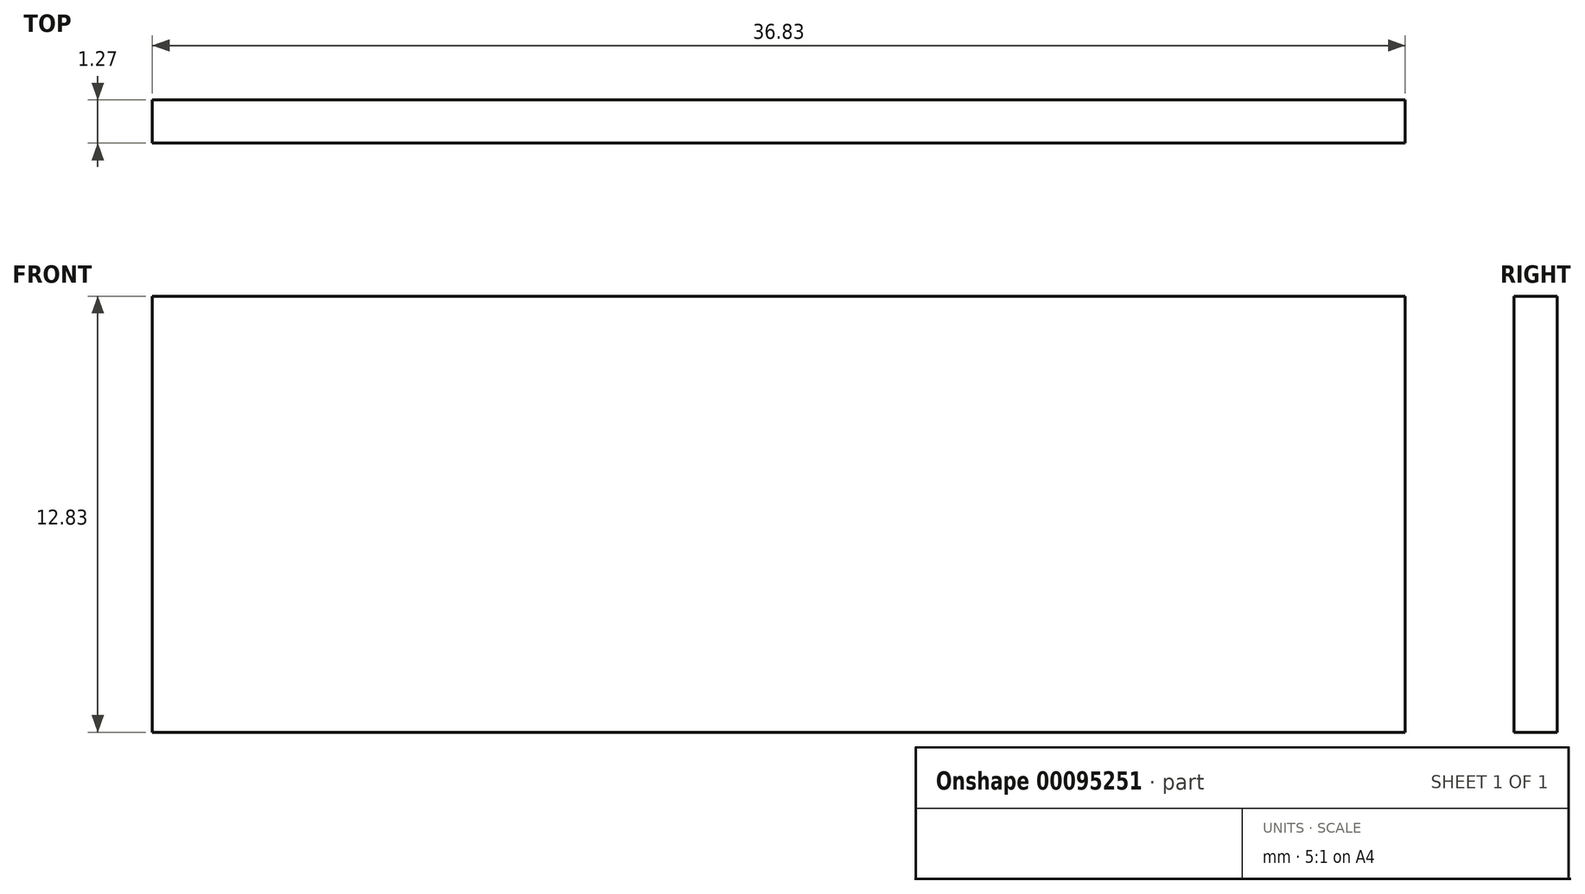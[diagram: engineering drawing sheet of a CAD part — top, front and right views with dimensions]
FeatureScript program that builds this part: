
annotation { "Feature Type Name" : "Feature", "Feature Type Description" : "" }
export const myFeature = defineFeature(function(context is Context, id is Id, definition is map)
    precondition{}
    {
        {
            var Q0;
            Q0=qCreatedBy(makeId("Front.planeOp"),FACE);
            var sketch = newSketch(context, id + "F0", { "sketchPlane" : qUnion([Q0])});
            skLineSegment(sketch, "E0.bottom", {"start": v(-21.73, 1.27) * mm, "end": v(15.1, 1.27) * mm});
            skLineSegment(sketch, "E0.top", {"start": v(-21.73, -11.56) * mm, "end": v(15.1, -11.56) * mm});
            skLineSegment(sketch, "E0.left", {"start": v(-21.73, 1.27) * mm, "end": v(-21.73, -11.56) * mm});
            skLineSegment(sketch, "E0.right", {"start": v(15.1, 1.27) * mm, "end": v(15.1, -11.56) * mm});
            skSolve(sketch);
        }
        {
            var Q0;
            Q0=makeQuery(id+"F0.imprint","IMPRINT",FACE,{"disambiguationData":[TD([[makeQuery(id+"F0.imprint","IMPRINT",EDGE,{"derivedFrom":sQuery(id+"F0.wireOp",EDGE,"E0.bottom")}),-1.0]])]});
            extrude(context, id + "F1", {"entities" : qUnion([Q0]), "depth" : 1.27 * mm});
        }
    });
